# Revit family: PLMx-xxxxx
name_source: partatom
category: Equipamento especial
units: mm (PartAtom-declared; Revit-internal decimal feet)

## family parameters
Com base no plano de trabalho = Não
Compartilhado = Não
Corte com vazios quando carregada = Não
Cota do conector redondo = Utilizar diâmetro
Número OmniClass = 23.40.40.14
Ponto de cálculo do ambiente = Não
Sempre na vertical = Sim
Tipo de parte = Normal
Título OmniClass = Food Service Equipment

## types (6) — shared parameters
Fabricante = MACOM
URL = https://www.acosmacom.com.br
zero-valued in all types: Elevação padrão

## per-type parameters (varying)
| type | Descrição | Height Actual | Length Actual | Middle Feet | Second Plate |
| PLM2-40238 | PRATELEIRA LISA SOBRE MONTANTES 2 PLANOS INOX MACOM-2380X400X850 | 850  [stored 2.78871 ft] | 2380  [stored 7.8084 ft] | Sim | Sim |
| PLM2-40188 | PRATELEIRA LISA SOBRE MONTANTES 2 PLANOS INOX MACOM-1880X400X850 | 850  [stored 2.78871 ft] | 1880  [stored 6.16798 ft] | Não | Sim |
| PLM2-40138 | PRATELEIRA LISA SOBRE MONTANTES 2 PLANOS INOX MACOM-1380X400X850 | 850  [stored 2.78871 ft] | 1380  [stored 4.52756 ft] | Não | Sim |
| PLM1-40238 | PRATELEIRA LISA SOBRE MONTANTES 1 PLANO INOX MACOM-2380X400X500 | 500  [stored 1.64042 ft] | 2380  [stored 7.8084 ft] | Sim | Não |
| PLM1-40188 | PRATELEIRA LISA SOBRE MONTANTES 1 PLANO INOX MACOM-1880X400X500 | 500  [stored 1.64042 ft] | 1880  [stored 6.16798 ft] | Não | Não |
| PLM1-40138 | PRATELEIRA LISA SOBRE MONTANTES 1 PLANO INOX MACOM-1380X400X500 | 500  [stored 1.64042 ft] | 1380  [stored 4.52756 ft] | Não | Não |

note: column(s) folded — value = type name in every type: Modelo

note: [stored X ft] marks values corroborated as IEEE doubles in the binary element streams (Revit-internal decimal feet)
